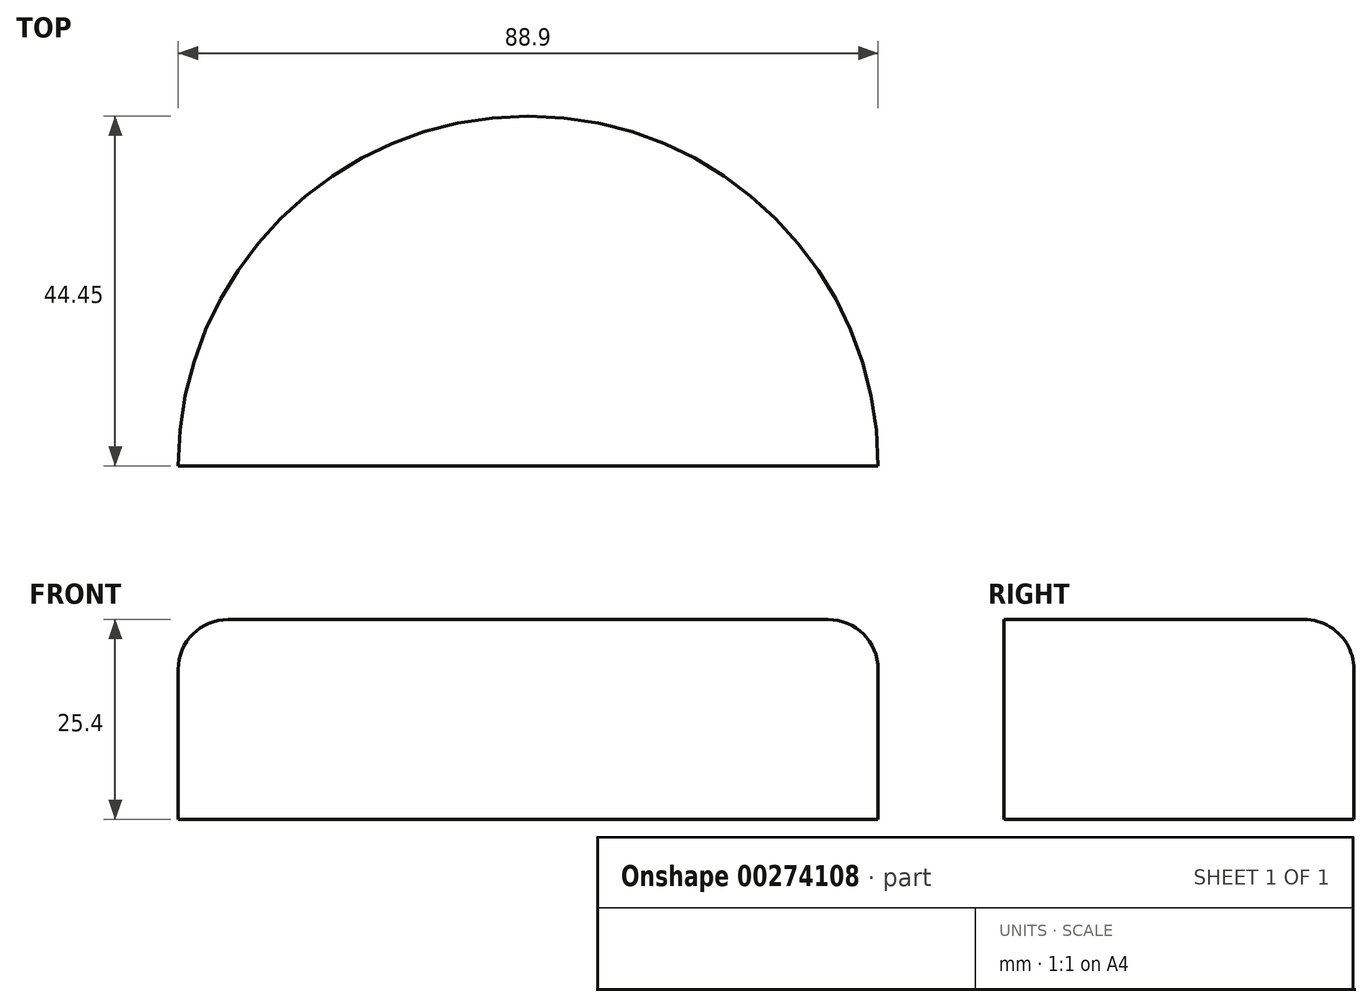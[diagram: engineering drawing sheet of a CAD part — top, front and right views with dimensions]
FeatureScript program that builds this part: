
annotation { "Feature Type Name" : "Feature", "Feature Type Description" : "" }
export const myFeature = defineFeature(function(context is Context, id is Id, definition is map)
    precondition{}
    {
        {
            var Q0;
            Q0=qCreatedBy(makeId("Top.planeOp"),FACE);
            var sketch = newSketch(context, id + "F0", { "sketchPlane" : qUnion([Q0])});
            skArc(sketch, "E0", {"start": v(-44.45, 0) * mm, "mid": v(0, 44.45) * mm, "end": v(44.45, 0) * mm});
            skLineSegment(sketch, "E1", {"start": v(-44.45, 0) * mm, "end": v(44.45, 0) * mm});
            skSolve(sketch);
        }
        {
            var Q0;
            Q0 = qSketchRegion(id + "F0", true);
            extrude(context, id + "F1", {"entities" : qUnion([Q0]), "depth" : 25.4 * mm});
        }
        {
            var Q0;
            Q0=makeQuery(id+"F1.opExtrude","CAP_EDGE",EDGE,{"disambiguationData":[OSD([sQuery(id+"F0.wireOp",EDGE,"E0")])],"isStart":false});
            fillet(context, id + "F2", {"entities" : qUnion([Q0]), "radius" : 6.35 * mm, "tangentPropagation" : true, "allowEdgeOverflow" : false});
        }
    });
